# Revit family: Electrical_Equipment-Floor_Box-Hubbell_Wiring-10_Gang-Concrete-CFB10G55R
name_source: partatom
category: Electrical Fixtures
revit_build: Autodesk Revit 2015 (Build: 20140606_1530(x64)
units: mm (PartAtom-declared; Revit-internal decimal feet)

## types (2) — shared parameters
Assembly Code = D5020115
Conduit Connector 1 Radius = 0.75 "
Conduit Connector 2 Radius = 0.625 "
Conduit Connector 3 Radius = 0.375 "
Conduit Connector 4 Radius = 0.625 "
Conduit Connector 5 Radius = 0.5 "
Conduit Connector 6 Radius = 0.25 "
Conduit Connector_1 Description = Conduit 1.5in, 1.25in. or 1in. Connection
Conduit Connector_10 Description = Conduit 0.75in. or 0.5in. Connection
Conduit Connector_11 Description = Conduit 1.0in, 0.75in. or 0.5in. Connection
Conduit Connector_12 Description = Conduit 1.0in, 0.75in. or 0.5in. Connection
Conduit Connector_13 Description = Conduit 1.0in, 0.75in. or 0.5in. Connection
Conduit Connector_14 Description = Conduit 1.0in, 0.75in. or 0.5in. Connection
Conduit Connector_15 Description = Conduit 0.5in. Connection
Conduit Connector_16 Description = Conduit 0.5in. Connection
Conduit Connector_2 Description = Conduit 1.5in, 1.25in. or 1in. Connection
Conduit Connector_3 Description = Conduit 1.25in, 1.0in. or 0.75in. Connection
Conduit Connector_4 Description = Conduit 1.25in, 1.0in. or 0.75in. Connection
Conduit Connector_5 Description = Conduit 0.75in. or 0.5in. Connection
Conduit Connector_6 Description = Conduit 0.75in. or 0.5in. Connection
Conduit Connector_7 Description = Conduit 0.75in. or 0.5in. Connection
Conduit Connector_8 Description = Conduit 0.75in. or 0.5in. Connection
Conduit Connector_9 Description = Conduit 0.75in. or 0.5in. Connection
Manufacturer = Hubbell-Wiring
Product data url = https://bimobject.com
URL = http://www.hubbell-wiring.com
zero-valued in all types: Default Elevation

## per-type parameters (varying)
| type | Box Material | Description | Product Documentation Link | Product Page URL |
| CFB10G55R | Metal - Hubbell - Steel | Concrete Floor Box, 10 Gang For 8'' Round Cover |  | http://www.hubbell-wiring.com |
| CFB10G55RCR | Metal - Hubbell - Green Finish | Concrete Floor Box, 10 Gang For 8'' Round Cover With Green Exterior | http://www.hubbell-wiring.com | http://ecatalog.hubbell-wiring.com |

note: column(s) folded — value = type name in every type: Model

## geometry (parser evidence)
native form markers: Blend x17, Sweep x8
no freeform markers — native parametric forms only
